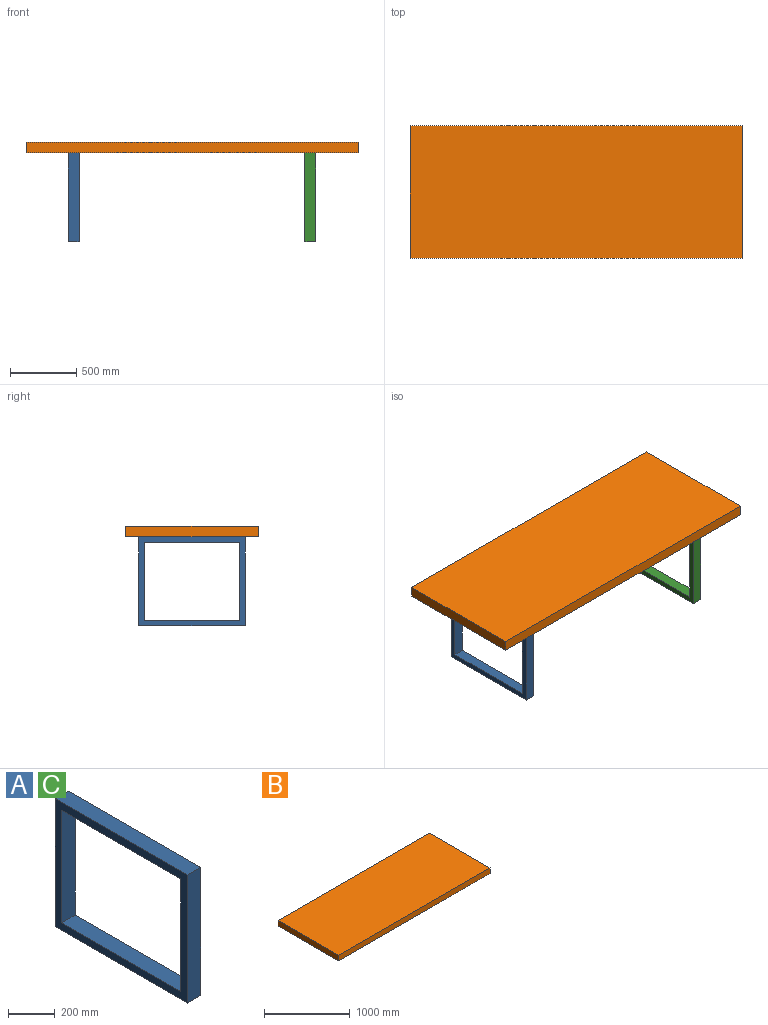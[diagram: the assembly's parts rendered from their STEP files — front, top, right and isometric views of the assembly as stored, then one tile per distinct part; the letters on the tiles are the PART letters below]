
ASSEMBLY  parts=3 mates=2
PART A: 10 faces, bbox 80x800x670 mm
  f0: plane 670x80mm, normal (0,1,0), area 53600mm2, adj f1,f7,f8,f9
  f1: plane 800x80mm, normal (0,0,1), area 64000mm2, adj f0,f2,f8,f9
  f2: plane 670x80mm, normal (0,-1,0), area 53600mm2, adj f1,f7,f8,f9
  f3: plane 590x80mm, normal (0,-1,0), area 47200mm2, adj f4,f6,f8,f9
  f4: plane 720x80mm, normal (0,0,1), area 57600mm2, adj f3,f5,f8,f9
  f5: plane 590x80mm, normal (0,1,0), area 47200mm2, adj f4,f6,f8,f9
  f6: plane 720x80mm, normal (0,0,-1), area 57600mm2, adj f3,f5,f8,f9
  f7: plane 800x80mm, normal (0,0,-1), area 64000mm2, adj f0,f2,f8,f9
  f8: plane 800x670mm, normal (1,0,0), area 111200mm2, adj f0,f1,f2,f3,f4,f5,f6,f7
  f9: plane 800x670mm, normal (-1,0,0), area 111200mm2, adj f0,f1,f2,f3,f4,f5,f6,f7
PART B: 6 faces, bbox 2500x1000x80 mm
  f0: plane 2500x80mm, normal (0,-1,0), area 200000mm2, adj f1,f3,f4,f5
  f1: plane 1000x80mm, normal (1,0,0), area 80000mm2, adj f0,f2,f4,f5
  f2: plane 2500x80mm, normal (0,1,0), area 200000mm2, adj f1,f3,f4,f5
  f3: plane 1000x80mm, normal (-1,0,0), area 80000mm2, adj f0,f2,f4,f5
  f4: plane 2500x1000mm, normal (0,0,1), area 2500000mm2, adj f0,f1,f2,f3
  f5: plane 2500x1000mm, normal (0,0,-1), area 2500000mm2, adj f0,f1,f2,f3
PART C: same geometry as A
PLACE A rot(axis=(0,0,1),180deg) t=(-731.75,0,-390.75)mm
PLACE B rot(axis=(0,-1,0),180deg) t=(118.25,0,24.25)mm
PLACE C rot(axis=(0,0,1),180deg) t=(1048.25,0,-390.75)mm
MATE fastened C.f1 <-> B.f4  axis (0,0,1) through (1008.25,0,-55.75)mm
MATE fastened A.f1 <-> B.f4  axis (0,0,1) through (-771.75,0,-55.75)mm
